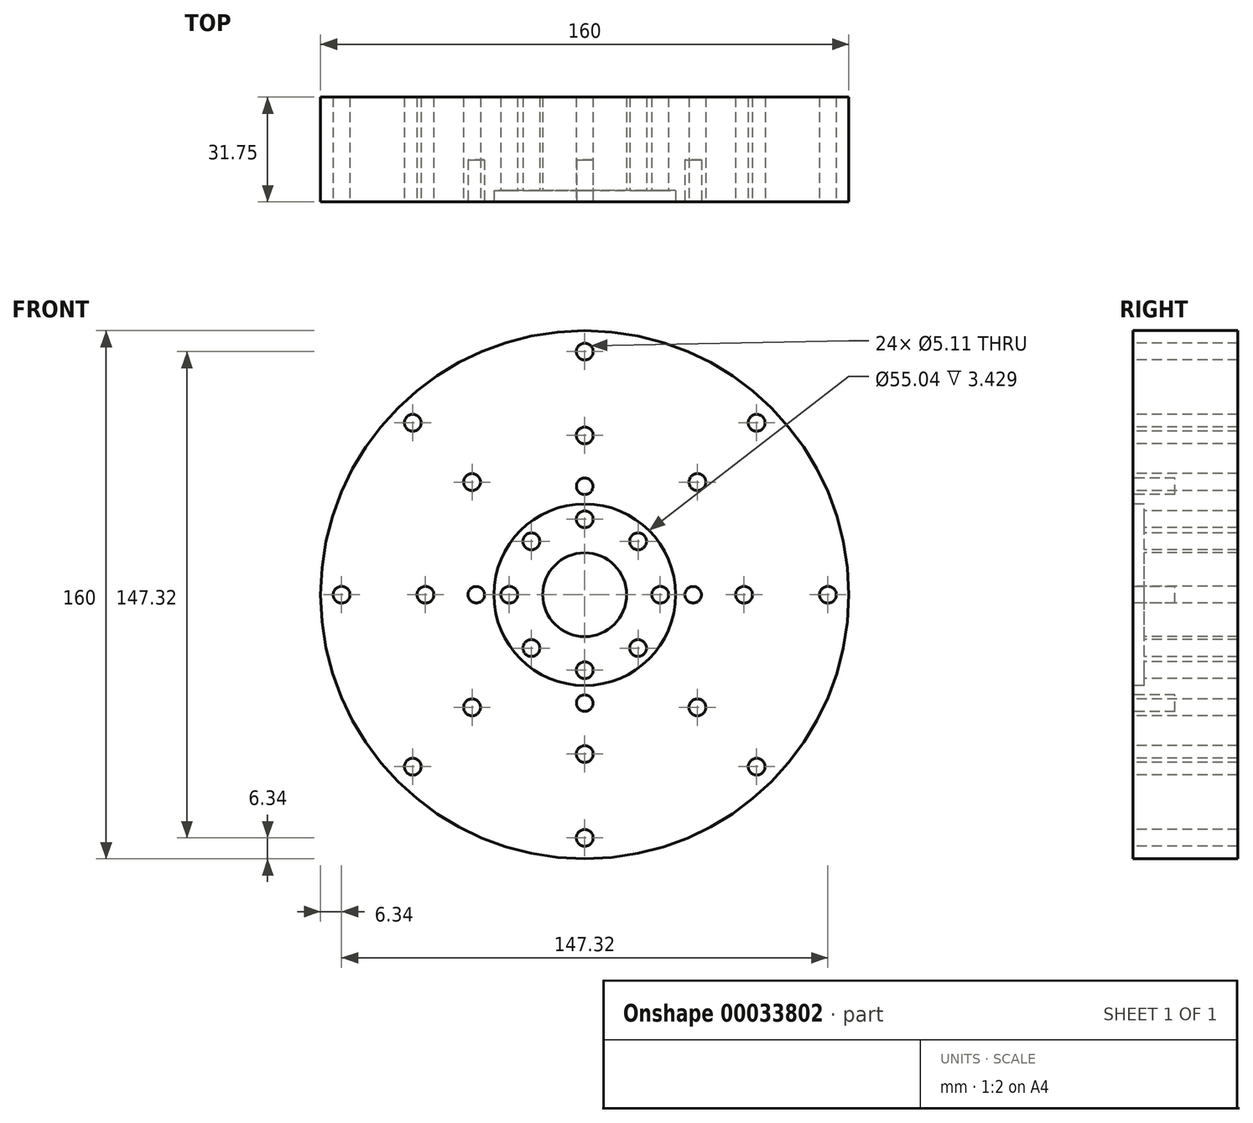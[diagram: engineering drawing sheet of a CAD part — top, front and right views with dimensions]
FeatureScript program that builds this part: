
annotation { "Feature Type Name" : "Feature", "Feature Type Description" : "" }
export const myFeature = defineFeature(function(context is Context, id is Id, definition is map)
    precondition{}
    {
        {
            var Q0;
            Q0=qCreatedBy(makeId("Front.planeOp"),FACE);
            var sketch = newSketch(context, id + "F0", { "sketchPlane" : qUnion([Q0])});
            skCircle(sketch, "E0", {"center": v(0, 0) * mm, "radius": 80 * mm});
            skCircle(sketch, "E1", {"center": v(0, 0) * mm, "radius": 12.7 * mm});
            skCircle(sketch, "E2", {"center": v(0, 0) * mm, "radius": 27.68 * mm, "construction": true});
            skCircle(sketch, "E3", {"center": v(0, 0) * mm, "radius": 27.52 * mm});
            skCircle(sketch, "E4", {"center": v(0, 0) * mm, "radius": 32.84 * mm, "construction": true});
            skCircle(sketch, "E5", {"center": v(0, 0) * mm, "radius": 39.98 * mm});
            skCircle(sketch, "E6", {"center": v(0, 32.84) * mm, "radius": 2.5 * mm});
            skCircle(sketch, "E7", {"center": v(-32.84, 0) * mm, "radius": 2.5 * mm});
            skCircle(sketch, "E8", {"center": v(32.84, 0) * mm, "radius": 2.5 * mm});
            skCircle(sketch, "E9", {"center": v(0, -32.84) * mm, "radius": 2.5 * mm});
            skCircle(sketch, "E10", {"center": v(-22.86, 0) * mm, "radius": 2.55 * mm});
            skCircle(sketch, "E11", {"center": v(-48.26, 0) * mm, "radius": 2.55 * mm});
            skCircle(sketch, "E12", {"center": v(-73.66, 0) * mm, "radius": 2.55 * mm});
            skCircle(sketch, "E13.1.0", {"center": v(-52.09, -52.09) * mm, "radius": 2.55 * mm});
            skCircle(sketch, "E13.1.1", {"center": v(-34.12, -34.12) * mm, "radius": 2.55 * mm});
            skCircle(sketch, "E13.1.2", {"center": v(-16.16, -16.16) * mm, "radius": 2.55 * mm});
            skCircle(sketch, "E13.2.0", {"center": v(0, -73.66) * mm, "radius": 2.55 * mm});
            skCircle(sketch, "E13.2.1", {"center": v(0, -48.26) * mm, "radius": 2.55 * mm});
            skCircle(sketch, "E13.2.2", {"center": v(0, -22.86) * mm, "radius": 2.55 * mm});
            skCircle(sketch, "E13.3.0", {"center": v(52.09, -52.09) * mm, "radius": 2.55 * mm});
            skCircle(sketch, "E13.3.1", {"center": v(34.12, -34.12) * mm, "radius": 2.55 * mm});
            skCircle(sketch, "E13.3.2", {"center": v(16.16, -16.16) * mm, "radius": 2.55 * mm});
            skCircle(sketch, "E13.4.0", {"center": v(73.66, 0) * mm, "radius": 2.55 * mm});
            skCircle(sketch, "E13.4.1", {"center": v(48.26, 0) * mm, "radius": 2.55 * mm});
            skCircle(sketch, "E13.4.2", {"center": v(22.86, 0) * mm, "radius": 2.55 * mm});
            skCircle(sketch, "E13.5.0", {"center": v(52.09, 52.09) * mm, "radius": 2.55 * mm});
            skCircle(sketch, "E13.5.1", {"center": v(34.12, 34.12) * mm, "radius": 2.55 * mm});
            skCircle(sketch, "E13.5.2", {"center": v(16.16, 16.16) * mm, "radius": 2.55 * mm});
            skCircle(sketch, "E13.6.0", {"center": v(0, 73.66) * mm, "radius": 2.55 * mm});
            skCircle(sketch, "E13.6.1", {"center": v(0, 48.26) * mm, "radius": 2.55 * mm});
            skCircle(sketch, "E13.6.2", {"center": v(0, 22.86) * mm, "radius": 2.55 * mm});
            skCircle(sketch, "E13.7.0", {"center": v(-52.09, 52.09) * mm, "radius": 2.55 * mm});
            skCircle(sketch, "E13.7.1", {"center": v(-34.12, 34.12) * mm, "radius": 2.55 * mm});
            skCircle(sketch, "E13.7.2", {"center": v(-16.16, 16.16) * mm, "radius": 2.55 * mm});
            skSolve(sketch);
        }
        {
            var Q0;
            Q0=makeQuery(id+"F0.imprint","IMPRINT",FACE,{"disambiguationData":[TD([[makeQuery(id+"F0.imprint","IMPRINT",EDGE,{"derivedFrom":sQuery(id+"F0.wireOp",EDGE,"E0")}),1.0]])]});
            var Q1;
            Q1=makeQuery(id+"F0.imprint","IMPRINT",FACE,{"disambiguationData":[TD([[makeQuery(id+"F0.imprint","IMPRINT",EDGE,{"derivedFrom":sQuery(id+"F0.wireOp",EDGE,"E5")}),1.0]])]});
            var Q2;
            Q2=makeQuery(id+"F0.imprint","IMPRINT",FACE,{"disambiguationData":[TD([[makeQuery(id+"F0.imprint","IMPRINT",EDGE,{"derivedFrom":sQuery(id+"F0.wireOp",EDGE,"E1")}),-1.0]])]});
            var Q3;
            Q3=makeQuery(id+"F0.imprint","IMPRINT",FACE,{"disambiguationData":[TD([[makeQuery(id+"F0.imprint","IMPRINT",EDGE,{"derivedFrom":sQuery(id+"F0.wireOp",EDGE,"E6")}),1.0]])]});
            var Q4;
            Q4=makeQuery(id+"F0.imprint","IMPRINT",FACE,{"disambiguationData":[TD([[makeQuery(id+"F0.imprint","IMPRINT",EDGE,{"derivedFrom":sQuery(id+"F0.wireOp",EDGE,"E9")}),1.0]])]});
            var Q5;
            Q5=makeQuery(id+"F0.imprint","IMPRINT",FACE,{"disambiguationData":[TD([[makeQuery(id+"F0.imprint","IMPRINT",EDGE,{"derivedFrom":sQuery(id+"F0.wireOp",EDGE,"E8")}),1.0]])]});
            var Q6;
            Q6=makeQuery(id+"F0.imprint","IMPRINT",FACE,{"disambiguationData":[TD([[makeQuery(id+"F0.imprint","IMPRINT",EDGE,{"derivedFrom":sQuery(id+"F0.wireOp",EDGE,"E7")}),1.0]])]});
            extrude(context, id + "F1", {"entities" : qUnion([Q0, Q1, Q2, Q3, Q4, Q5, Q6]), "oppositeDirection" : true, "depth" : 31.75 * mm});
        }
        {
            var Q0;
            Q0=makeQuery(id+"F0.imprint","IMPRINT",FACE,{"disambiguationData":[TD([[makeQuery(id+"F0.imprint","IMPRINT",EDGE,{"derivedFrom":sQuery(id+"F0.wireOp",EDGE,"E6")}),1.0]])]});
            var Q1;
            Q1=makeQuery(id+"F0.imprint","IMPRINT",FACE,{"disambiguationData":[TD([[makeQuery(id+"F0.imprint","IMPRINT",EDGE,{"derivedFrom":sQuery(id+"F0.wireOp",EDGE,"E8")}),1.0]])]});
            var Q2;
            Q2=makeQuery(id+"F0.imprint","IMPRINT",FACE,{"disambiguationData":[TD([[makeQuery(id+"F0.imprint","IMPRINT",EDGE,{"derivedFrom":sQuery(id+"F0.wireOp",EDGE,"E9")}),1.0]])]});
            var Q3;
            Q3=makeQuery(id+"F0.imprint","IMPRINT",FACE,{"disambiguationData":[TD([[makeQuery(id+"F0.imprint","IMPRINT",EDGE,{"derivedFrom":sQuery(id+"F0.wireOp",EDGE,"E7")}),1.0]])]});
            var Q4;
            Q4=sQuery(id+"F0.wireOp",EDGE,"E8");
            var Q5;
            Q5=sQuery(id+"F0.wireOp",EDGE,"E6");
            var Q6;
            Q6=sQuery(id+"F0.wireOp",EDGE,"E7");
            var Q7;
            Q7=sQuery(id+"F0.wireOp",EDGE,"E9");
            extrude(context, id + "F2", {"entities" : qUnion([Q0, Q1, Q2, Q3]), "operationType" : NewBodyOperationType.REMOVE, "surfaceEntities" : qUnion([Q4, Q5, Q6, Q7]), "oppositeDirection" : true, "depth" : 12.7 * mm});
        }
        {
            var Q0;
            Q0=makeQuery(id+"F0.imprint","IMPRINT",FACE,{"disambiguationData":[TD([[makeQuery(id+"F0.imprint","IMPRINT",EDGE,{"derivedFrom":sQuery(id+"F0.wireOp",EDGE,"E1")}),-1.0]])]});
            var Q1;
            {var subQ0=sQuery(id+"F0.wireOp",EDGE,"E13.5.2");var subQ1=sQuery(id+"F0.wireOp",EDGE,"E3");var subQ3=makeQuery(id+"F0.imprint","INTERSECT",VERTEX,{"disambiguationData":[OD(0.0)],"derivedFrom":[subQ1,subQ0]});Q1=makeQuery(id+"F0.imprint","IMPRINT",FACE,{"disambiguationData":[TD([[makeQuery(id+"F0.imprint","IMPRINT",EDGE,{"disambiguationData":[TD([[subQ3,-1.0]])],"derivedFrom":subQ1}),1.0]])]});}
            var Q2;
            {var subQ0=sQuery(id+"F0.wireOp",EDGE,"E13.4.2");var subQ1=sQuery(id+"F0.wireOp",EDGE,"E3");var subQ3=makeQuery(id+"F0.imprint","INTERSECT",VERTEX,{"disambiguationData":[OD(0.0)],"derivedFrom":[subQ1,subQ0]});Q2=makeQuery(id+"F0.imprint","IMPRINT",FACE,{"disambiguationData":[TD([[makeQuery(id+"F0.imprint","IMPRINT",EDGE,{"disambiguationData":[TD([[subQ3,1.0]])],"derivedFrom":subQ1}),1.0]])]});}
            var Q3;
            {var subQ0=sQuery(id+"F0.wireOp",EDGE,"E13.3.2");var subQ1=sQuery(id+"F0.wireOp",EDGE,"E3");var subQ3=makeQuery(id+"F0.imprint","INTERSECT",VERTEX,{"disambiguationData":[OD(0.0)],"derivedFrom":[subQ1,subQ0]});Q3=makeQuery(id+"F0.imprint","IMPRINT",FACE,{"disambiguationData":[TD([[makeQuery(id+"F0.imprint","IMPRINT",EDGE,{"disambiguationData":[TD([[subQ3,-1.0]])],"derivedFrom":subQ1}),1.0]])]});}
            var Q4;
            {var subQ0=sQuery(id+"F0.wireOp",EDGE,"E13.2.2");var subQ1=sQuery(id+"F0.wireOp",EDGE,"E3");var subQ3=makeQuery(id+"F0.imprint","INTERSECT",VERTEX,{"disambiguationData":[OD(0.0)],"derivedFrom":[subQ1,subQ0]});Q4=makeQuery(id+"F0.imprint","IMPRINT",FACE,{"disambiguationData":[TD([[makeQuery(id+"F0.imprint","IMPRINT",EDGE,{"disambiguationData":[TD([[subQ3,-1.0]])],"derivedFrom":subQ1}),1.0]])]});}
            var Q5;
            {var subQ0=sQuery(id+"F0.wireOp",EDGE,"E13.1.2");var subQ1=sQuery(id+"F0.wireOp",EDGE,"E3");var subQ3=makeQuery(id+"F0.imprint","INTERSECT",VERTEX,{"disambiguationData":[OD(0.0)],"derivedFrom":[subQ1,subQ0]});Q5=makeQuery(id+"F0.imprint","IMPRINT",FACE,{"disambiguationData":[TD([[makeQuery(id+"F0.imprint","IMPRINT",EDGE,{"disambiguationData":[TD([[subQ3,-1.0]])],"derivedFrom":subQ1}),1.0]])]});}
            var Q6;
            {var subQ0=sQuery(id+"F0.wireOp",EDGE,"E10");var subQ1=sQuery(id+"F0.wireOp",EDGE,"E3");var subQ3=makeQuery(id+"F0.imprint","INTERSECT",VERTEX,{"disambiguationData":[OD(0.0)],"derivedFrom":[subQ1,subQ0]});Q6=makeQuery(id+"F0.imprint","IMPRINT",FACE,{"disambiguationData":[TD([[makeQuery(id+"F0.imprint","IMPRINT",EDGE,{"disambiguationData":[TD([[subQ3,-1.0]])],"derivedFrom":subQ1}),1.0]])]});}
            var Q7;
            {var subQ0=sQuery(id+"F0.wireOp",EDGE,"E13.7.2");var subQ1=sQuery(id+"F0.wireOp",EDGE,"E3");var subQ3=makeQuery(id+"F0.imprint","INTERSECT",VERTEX,{"disambiguationData":[OD(0.0)],"derivedFrom":[subQ1,subQ0]});Q7=makeQuery(id+"F0.imprint","IMPRINT",FACE,{"disambiguationData":[TD([[makeQuery(id+"F0.imprint","IMPRINT",EDGE,{"disambiguationData":[TD([[subQ3,-1.0]])],"derivedFrom":subQ1}),1.0]])]});}
            var Q8;
            {var subQ0=sQuery(id+"F0.wireOp",EDGE,"E13.6.2");var subQ1=sQuery(id+"F0.wireOp",EDGE,"E3");var subQ3=makeQuery(id+"F0.imprint","INTERSECT",VERTEX,{"disambiguationData":[OD(0.0)],"derivedFrom":[subQ1,subQ0]});Q8=makeQuery(id+"F0.imprint","IMPRINT",FACE,{"disambiguationData":[TD([[makeQuery(id+"F0.imprint","IMPRINT",EDGE,{"disambiguationData":[TD([[subQ3,-1.0]])],"derivedFrom":subQ1}),1.0]])]});}
            extrude(context, id + "F3", {"entities" : qUnion([Q0, Q1, Q2, Q3, Q4, Q5, Q6, Q7, Q8]), "operationType" : NewBodyOperationType.REMOVE, "oppositeDirection" : true, "depth" : 3.43 * mm});
        }
    });
